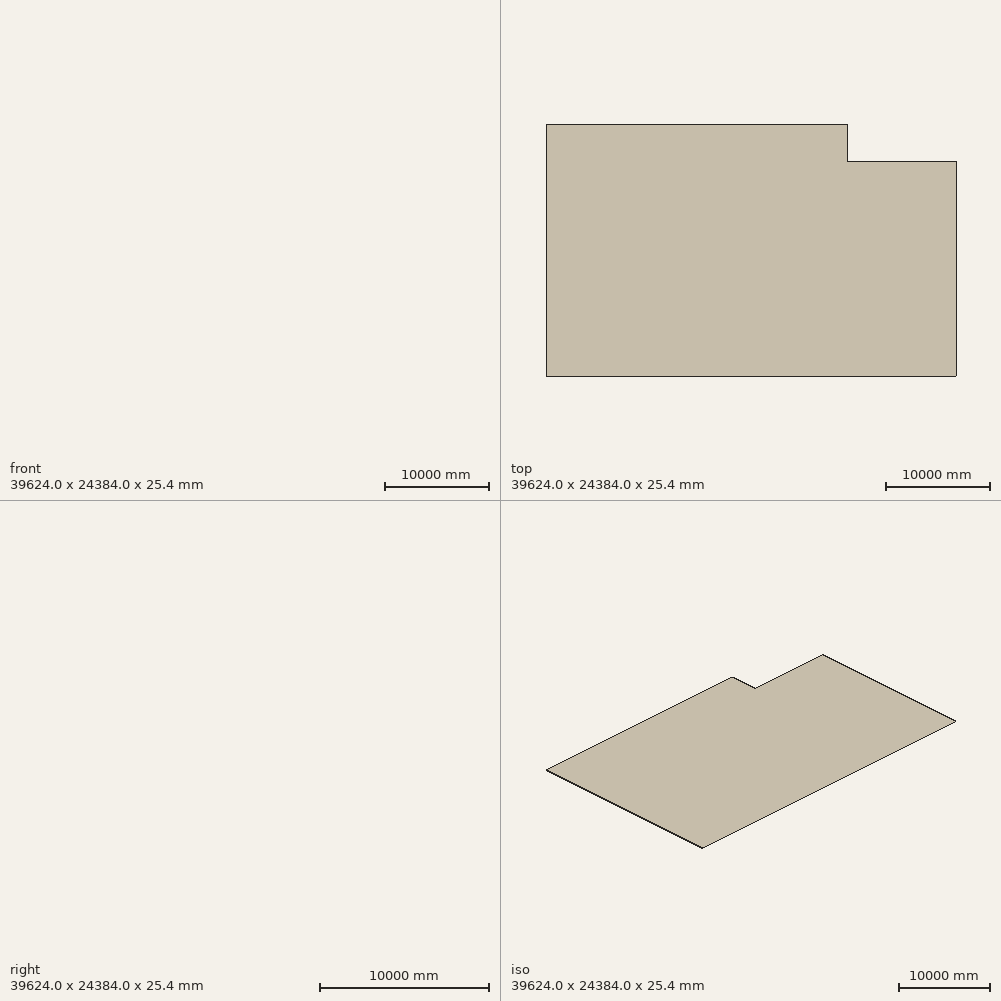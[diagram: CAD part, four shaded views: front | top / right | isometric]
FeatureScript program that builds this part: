
annotation { "Feature Type Name" : "Feature", "Feature Type Description" : "" }
export const myFeature = defineFeature(function(context is Context, id is Id, definition is map)
    precondition{}
    {
        {
            var Q0;
            Q0=qCreatedBy(makeId("Top.planeOp"),FACE);
            var sketch = newSketch(context, id + "F0", { "sketchPlane" : qUnion([Q0])});
            skLineSegment(sketch, "E0", {"start": v(0, 0) * mm, "end": v(-39624, 0) * mm});
            skLineSegment(sketch, "E1", {"start": v(-39624, 0) * mm, "end": v(-39624, 24384) * mm});
            skLineSegment(sketch, "E2", {"start": v(-39624, 24384) * mm, "end": v(-10566.4, 24384) * mm});
            skLineSegment(sketch, "E3", {"start": v(-10566.4, 24384) * mm, "end": v(-10566.4, 20834.6) * mm});
            skLineSegment(sketch, "E4", {"start": v(-10566.4, 20834.6) * mm, "end": v(0, 20834.6) * mm});
            skLineSegment(sketch, "E5", {"start": v(0, 20834.6) * mm, "end": v(0, 0) * mm});
            skSolve(sketch);
        }
        {
            var Q0;
            Q0 = qSketchRegion(id + "F0", true);
            extrude(context, id + "F1", {"entities" : qUnion([Q0]), "depth" : 25.4 * mm, "offsetDistance" : 25.4 * mm});
        }
    });
